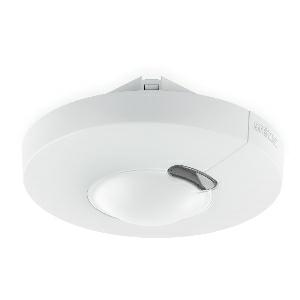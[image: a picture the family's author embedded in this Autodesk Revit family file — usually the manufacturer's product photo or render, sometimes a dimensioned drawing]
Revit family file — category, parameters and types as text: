
# Revit family: hf_3360_033750
name_source: partatom
category: Elektroinstallationen
revit_build: Autodesk Revit 2016 (Build: 20190508_0715(x64)
units: mm (PartAtom-declared; Revit-internal decimal feet)

## family parameters
Basisbauteil = Fläche
Beim Laden mit Abzugskörper schneiden = Nein
Bemaßung runder Anschluss = Durchmesser verwenden
Beschriftungsausrichtung beibehalten = Nein
Gemeinsam genutzt = Nein
Raumberechnungspunkt = Nein
Teiletyp = Normal

## types (1)
- HF 3360
    Apparent Load = 0 VA
    Beschreibung = Type: Motion detectors; Dimensions (Ø x H): 124 x 64 mm; Mains power supply: 220 – 240 V / 50 – 60 Hz; Sensor Technology: High frequency; Application, place: Indoors; Application, room: function room / ancillary room, stairwell, WC / washroom, multi-storey / underground car park, Indoors; Installation site: wall, ceiling, corner; Installation: Concealed wiring; HF-system: 5,8 GHz; Electronic scalability: Yes; Mechanical scalability: No; Mounting height: 2,00 – 4,00 m; Optimum mounting height: 2,8 m; Detection: also through glass, wood and stud walls; Detection angle: 360 °; Angle of aperture: 140 °; Sneak-by guard: Yes; Reach, radial: Ø 8 m (50 m²); Reach, tangential: Ø 8 m (50 m²); Twilight setting TEACH: Yes; Twilight setting: 2 – 1000 lx; Time setting: 5 sec – 15 min; Control output, Dali: Broadcast 1x30 electronic ballasts; Constant-lighting control: Yes; Basic light level function: Yes; Basic light level function in per cent: 10 – 50 %; Basic light level function time: 1-30 min, all night; Basic light level function percentage, from: 10 %; Basic light level function percentage, up to: 50 %; Functions: Normal / test mode, Manual ON / ON-OFF, Constant-lighting control ON-OFF; Settings via: Remote control, Potentiometers, Smart Remote; With remote control: No; Interconnection: Yes; IP-rating: IP20; Material: Plastic; Ambient temperature: -20 – 50 °C; Colour: white; Colour, RAL: 9003; Manufacturer's Warranty: 5 years; Version: DALI-2 Application Controller - concealed, rd.; PU1, EAN: 4007841033750
    Height = 0 mm  [stored 0 ft]
    Hersteller = Steinel
    Length = 124 mm  [stored 0.406824 ft]
    ModVariant = Nein
    Modell = 033750
    Mounting Type = Recessed
    Number of Poles = 1
    OnlyDefault = Ja
    Power Factor = 1
    Product Name = HF 3360
    Product group = Sensor-switched indoor light
    ProductGroupID = 30
    Protection Class = Protection class
    Protection Degree = IP 20
    RlxData = <blob elided: 36773 chars, md5=bd3f2fe5>
    SensorDataFile = {"IESDataFiles":[]}
    Typenbild = produkt1_033750.jpg
    Typenkommentare = Product without accessories
    URL = http://relux.com
    VarID = ---
    Voltage = 0 V
    Vorgabe-Ansicht = 1800 mm
    Weight = 0.00 kg
    Width = 0 mm  [stored 0 ft]

note: [stored X ft] marks values corroborated as IEEE doubles in the binary element streams (Revit-internal decimal feet)

## geometry (parser evidence)
native form markers: Sweep x13
no freeform markers — native parametric forms only
